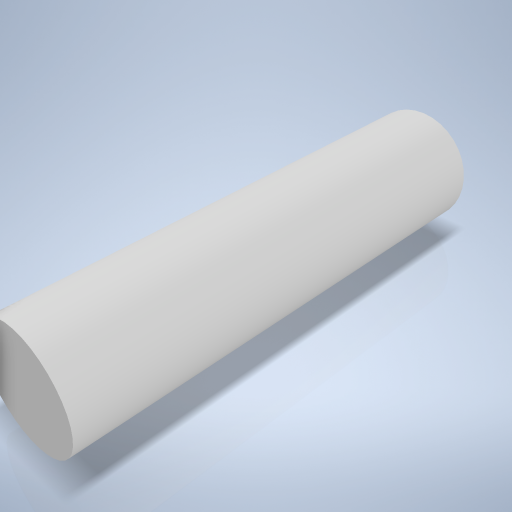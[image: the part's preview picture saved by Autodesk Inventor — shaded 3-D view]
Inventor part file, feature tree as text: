
AUTODESK INVENTOR PART (.ipt)
format: ipt  version: 2024.2 (Build 282272000, 272)  size: 219,136 bytes
history: native  units: mm
features: extrude x1, sketch x1
ambient origin geometry x8: Origin, YZ Plane, XZ Plane, XY Plane, X Axis, Y Axis, Z Axis, Center Point
bodies: Volumenkörper1 (feature_tree)
feature tree (2):
  extrude  "Extrusion1"  Depth=8.0mm TaperAngle=0.0deg
  sketch  "Skizze1"  dims[d0=2.0mm d1=8.0mm d2=0.0mm]
